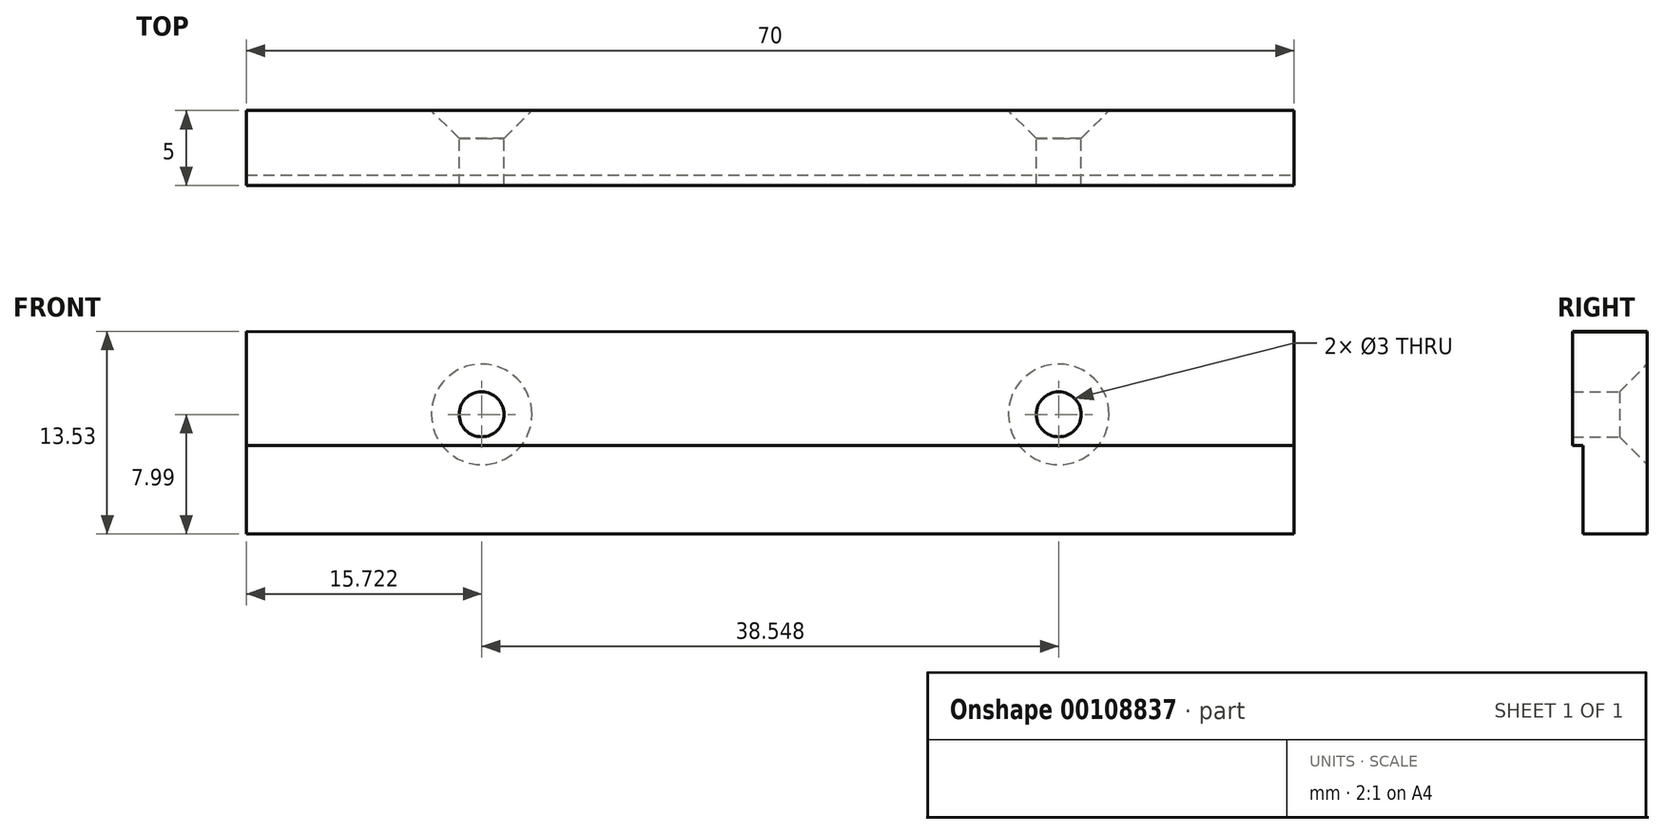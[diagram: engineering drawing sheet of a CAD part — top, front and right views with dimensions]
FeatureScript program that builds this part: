
annotation { "Feature Type Name" : "Feature", "Feature Type Description" : "" }
export const myFeature = defineFeature(function(context is Context, id is Id, definition is map)
    precondition{}
    {
        {
            var Q0;
            Q0=qCreatedBy(makeId("Front.planeOp"),FACE);
            var sketch = newSketch(context, id + "F0", { "sketchPlane" : qUnion([Q0])});
            skLineSegment(sketch, "E0", {"start": v(-37.22, 0) * mm, "end": v(37.27, 0) * mm, "construction": true});
            skLineSegment(sketch, "E1", {"start": v(-18.9, 4.81) * mm, "end": v(-18.9, -16.86) * mm, "construction": true});
            skLineSegment(sketch, "E2", {"start": v(19.65, 6.41) * mm, "end": v(19.65, -17.16) * mm, "construction": true});
            skLineSegment(sketch, "E3", {"start": v(-34.62, 6.11) * mm, "end": v(-34.62, -13.06) * mm, "construction": true});
            skLineSegment(sketch, "E4", {"start": v(35.38, 5.51) * mm, "end": v(35.38, -14.26) * mm, "construction": true});
            skPoint(sketch, "E5", {"position": v(-18.9, 0) * mm});
            skPoint(sketch, "E6", {"position": v(19.65, 0) * mm});
            skLineSegment(sketch, "E7", {"start": v(-34.62, 0) * mm, "end": v(-34.62, 5.54) * mm});
            skLineSegment(sketch, "E8", {"start": v(-34.62, 5.54) * mm, "end": v(35.38, 5.51) * mm});
            skLineSegment(sketch, "E9", {"start": v(35.38, 0) * mm, "end": v(35.38, -8) * mm});
            skLineSegment(sketch, "E10", {"start": v(35.38, -8) * mm, "end": v(-34.62, -8) * mm});
            skLineSegment(sketch, "E11", {"start": v(-34.62, -8) * mm, "end": v(-34.62, 0) * mm});
            skLineSegment(sketch, "E12", {"start": v(-34.62, -2.1) * mm, "end": v(35.38, -2.1) * mm});
            skLineSegment(sketch, "E13", {"start": v(35.38, 5.51) * mm, "end": v(35.38, -2.1) * mm});
            skSolve(sketch);
        }
        {
            var Q0;
            {var subQ2=sQuery(id+"F0.wireOp",EDGE,"E7");Q0=makeQuery(id+"F0.imprint","IMPRINT",FACE,{"disambiguationData":[TD([[makeQuery(id+"F0.imprint","IMPRINT",EDGE,{"derivedFrom":subQ2}),-1.0]])]});}
            extrude(context, id + "F1", {"entities" : qUnion([Q0]), "depth" : 5 * mm});
        }
        {
            var Q0;
            Q0=makeQuery(id+"F0.imprint","IMPRINT",FACE,{"disambiguationData":[TD([[makeQuery(id+"F0.imprint","IMPRINT",EDGE,{"derivedFrom":sQuery(id+"F0.wireOp",EDGE,"E9")}),-1.0]])]});
            extrude(context, id + "F2", {"entities" : qUnion([Q0]), "operationType" : NewBodyOperationType.ADD, "depth" : 4.3 * mm});
        }
        {
            var Q0;
            Q0=sQuery(id+"F0.wireOp",VERTEX,"E6");
            var Q1;
            Q1=sQuery(id+"F0.wireOp",VERTEX,"E5");
            var Q2;
            Q2=makeQuery(id+"F1.opExtrude","SWEPT_BODY",BODY,{"disambiguationData":[OSD([sQuery(id+"F0.wireOp",EDGE,"E7"),sQuery(id+"F0.wireOp",EDGE,"E8"),sQuery(id+"F0.wireOp",EDGE,"E11"),sQuery(id+"F0.wireOp",EDGE,"E12"),sQuery(id+"F0.wireOp",EDGE,"E13")])]});
            hole(context, id + "F3", {"style" : HoleStyle.C_SINK, "endStyle" : HoleEndStyle.THROUGH, "oppositeDirection" : true, "standardTappedOrClearance" : lookupTablePath({ "standard" : "ISO", "size" : "3", "type" : "Drilled" }), "standardBlindInLast" : lookupTablePath({ "standard" : "ISO", "size" : "3", "type" : "Drilled" }), "holeDiameter" : 3 * mm, "cSinkDiameter" : 6.72 * mm, "cSinkAngle" : 90 * degree, "startFromSketch" : true, "locations" : qUnion([Q0, Q1]), "scope" : qUnion([Q2]), "isTappedThrough" : true});
        }
    });
